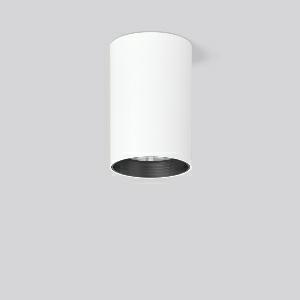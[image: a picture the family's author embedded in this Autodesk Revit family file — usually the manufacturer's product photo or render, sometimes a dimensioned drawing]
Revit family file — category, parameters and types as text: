
# Revit family: heledon_maxi_a_931250_002_2_2705
name_source: partatom
category: Lighting Fixtures
units: mm (PartAtom-declared; Revit-internal decimal feet)

## family parameters
Cut with Voids When Loaded = No
Host = Face
Light Source = No
Part Type = Normal
Room Calculation Point = No
Round Connector Dimension = Use Diameter
Shared = No

## types (1)
- HELEDON maxi A (1 x LED Modul 927 bakery, 2900 lm, 2700)
    Apparent Load = 33 VA
    Approval mark = CE
    CIE Flux Codes = 96 99 100 100 100
    Color Rendering = 90
    Color Temperature = 2700
    Default Elevation = 1800 mm
    Description = Series: HELEDON maxi
Cylindrical surface-mounted downlight. Housing: die-cast aluminium, powder-coated. Internal ceiling frame polycarbonate with bayonet mounting. Black plastic ring and recessed LED to prevent glare from the side. Optical assembly with lens made of plastic (polycarbonate) for the best homogeneous light distribution - can be changed without tools. Special LED for illumination of pastries included. Suitable for Ceiling mounting. Easy installation with a separate ceiling frame with bayonet mounting and plug connection. Driver integrated. Connected via plug-in connector. High quality converter without flickering and stroboscopic effect. The following accessories can be mounted without use of tools: interchangeable lenses, decorative glasses, honeycomb louvre, clear and frosted diffusers, white interchangeable plastic ring. 
Colour: traffic white, matt (RAL 9016)
Diameter: 123 mm
Height: 183 mm
Lamp: LED
Socket: without socket
Colour temperature: bakery
Colour rendering index (CRI): 97
System power: 33 W
Rated luminous flux: 2900 lm
Luminous efficiency: 88 lm/W
Control gear: Regulated power supply
Protection class: I
Type of protection: IP 20
    Height = 183 mm
    Lamp = 1 x LED Modul 927 bakery
    Lamp Light Flux = 2900 lm
    Lamp count = 1
    Length = 123 mm
    Lifetime = 50000 h
    Luminous efficacy = 88 lm/W
    Manufacturer = RZB
    ModVariant = No
    Model = 931250.002.2
    Mounting Place = Ceiling
    Mounting Type = Surface mounted
    Number of Poles = 1
    OnlyDefault = Yes
    Power Factor = 1
    Product Name = HELEDON maxi A
    Product group = Surface mounted downlights
    ProductGroupID = 302
    Protection Class = Protection class I
    Protection Degree = IP 20
    RLX_Detail_Level = 1
    RLX_Emergency_Light_Flux = 0 lm
    RLX_Emergency_Type = 0
    RLX_Emergency_Type_DB = No
    RlxData = <blob elided: 97965 chars, md5=7c3f28d0>
    Socket = socket
    Standby Power = 0 W
    System Light Flux = 2900 lm
    System Power = 33 W
    Type Comments = Product without accessories
    Type Image = 931193.002.jpg
    URL = http://relux.com
    VarID = ---
    Voltage = 230 V
    Voltage Range = 220-240 V
    Weight = 0.00 kg
    Width = 0 mm  [stored 0 ft]

note: [stored X ft] marks values corroborated as IEEE doubles in the binary element streams (Revit-internal decimal feet)

## geometry (parser evidence)
native form markers: Blend x4, Sweep x10
no freeform markers — native parametric forms only
